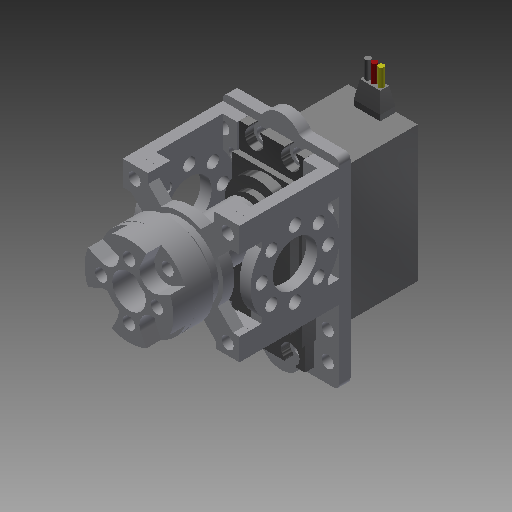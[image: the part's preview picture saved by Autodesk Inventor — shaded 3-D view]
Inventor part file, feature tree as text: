
AUTODESK INVENTOR PART (.ipt)
format: ipt  version: 2019 (Build 230136000, 136)  size: 800,768 bytes
history: native  units: in
note: dims shown in document units (in); Inventor stores cm internally (conversion verified against a paired STEP export)
features: extrude x23, sketch x23, other x11, projected_geometry x10, fillet x3, mirror x2, plane x1, pattern_circular x1
ambient origin geometry x8: Origin, YZ Plane, XZ Plane, XY Plane, X Axis, Y Axis, Z Axis, Center Point
bodies: Body1 (feature_tree), Body2 (feature_tree), Body3 (feature_tree), Body4 (feature_tree), Body5 (feature_tree), Body6 (feature_tree), Body7 (feature_tree), Body8 (feature_tree), Body9 (feature_tree), Body10 (feature_tree)
feature tree (74):
  other  "Servo"
  extrude  "Extrusion1"  Depth=1.525in
  extrude  "Extrusion2"  Depth=0.025in
  extrude  "Extrusion3"  Depth=0.17in
  fillet  "Fillet1"  Radius=0.11in
  plane  "Work Plane1"
  extrude  "Extrusion4"  Depth=0.07in
  fillet  "Fillet2"  Radius=0.07in
  mirror  "Mirror1"
  extrude  "Extrusion5"  [1 undecoded]
  extrude  "Extrusion6"  Depth=0.28in
  extrude  "Extrusion7"  Depth=0.1in
  extrude  "Extrusion8"  Depth=0.1in TaperAngle=0.0deg
  extrude  "Extrusion9"  Depth=0.3in
  extrude  "Extrusion10"  Depth=0.01in
  fillet  "Fillet3"  Radius=0.0625in
  extrude  "Extrusion11"  Depth=0.0625in
  extrude  "Extrusion12"  Depth=0.0625in
  extrude  "Extrusion13"  Depth=0.2in TaperAngle=0.0deg
  extrude  "Extrusion14"  Depth=0.0625in
  extrude  "Extrusion15"  Depth=0.2in
  extrude  "Extrusion16"  Depth=0.125in
  mirror  "Mirror2"
  extrude  "Extrusion18"  Depth=0.25in
  extrude  "Extrusion19"  Depth=0.125in
  extrude  "Extrusion20"  Depth=0.1325in
  extrude  "Extrusion21"  Depth=1.3125in
  extrude  "Extrusion22"  Depth=0.125in TaperAngle=0.0deg
  extrude  "Extrusion23"  Depth=0.125in
  extrude  "Extrusion24"  Depth=0.083in
  pattern_circular  "Circular Pattern1"  [2 undecoded]
  sketch  "Sketch1"  dims[d0=0.782in d1=1.525in]
  sketch  "Sketch2"  dims[d2=1.305in d3=0.0in d4=0.025in]
  sketch  "Sketch3"  dims[d5=0.025in d6=0.17in d7=0.11in d8=0.0in]
  sketch  "Sketch4"  dims[d9=0.508in d11=0.391in d12=0.07in d13=0.0in]
  sketch  "Sketch5"  dims[d14=0.366in d15=-0.16in]
  sketch  "Sketch6"  dims[d16=0.737in d18=0.28in]
  sketch  "Sketch7"  dims[d19=0.1in d20=0.21in d21=0.165in]
  other  "Red wire"
  sketch  "Sketch8"  dims[d22=0.165in d23=0.1in d24=0.0in]
  sketch  "Sketch9"  dims[d25=0.01in d26=0.3in]
  other  "Yellow Wire"
  sketch  "Sketch10"  dims[d27=0.17in d28=0.01in d29=0.0625in d30=0.0in]
  other  "BaseStructure"
  sketch  "Sketch11"  dims[d31=0.2in d32=-0.0687in d33=0.0625in]
  other  "ServoOutput"
  sketch  "Sketch12"  dims[d34=0.2in d35=0.0in d36=0.0625in]
  other  "SideStructure"
  sketch  "Sketch13"  dims[d37=0.04in d38=0.2in d39=0.0in]
  sketch  "Sketch14"  dims[d40=0.0625in d41=0.04in]
  projected_geometry  "Projected Loop1"
  projected_geometry  "Projected Loop2"
  sketch  "Sketch16"  dims[d42=0.2in d43=0.0in d44=0.136in]
  sketch  "Sketch17"  dims[d47=2.25in d48=0.125in]
  other  "Pattern of SideStructure:1"
  other  "SideStructureMirror"
  sketch  "Sketch18"  dims[d49=0.25in d50=0.25in]
  projected_geometry  "Projected Loop3"
  projected_geometry  "Projected Loop4"
  projected_geometry  "Projected Loop5"
  projected_geometry  "Projected Loop6"
  projected_geometry  "Projected Loop7"
  other  "BearingStructure"
  sketch  "Sketch19"  dims[d51=0.125in d52=0.2165in]
  sketch  "Sketch20"  dims[d53=0.1325in d54=0.1325in]
  other  "HubShaft"
  sketch  "Sketch21"  dims[d55=1.3125in d56=0.3125in]
  sketch  "Sketch22"  dims[d57=0.435in d58=0.125in d59=0.0in]
  sketch  "Sketch23"  dims[d60=0.0625in d61=0.125in]
  other  "HubAdapter"
  sketch  "Sketch24"  dims[d62=0.0625in d63=0.0in d66=0.083in d67=0.083in d68=0.125in d69=0.125in d70=0.125in d71=0.0in d72=0.125in d73=0.75in d74=0.0in d75=0.125in d76=0.0in d80=1.0in d82=0.125in d83=0.0in d84=0.5in d85=0.75in d86=0.136in d87=3.1496in d89=360.0deg d91=0.125in d92=0.0in d93=0.95in d94=45.0deg d96=0.26in d97=0.13in d100=45.0deg d101=0.13in d102=0.26in d103=0.125in d104=0.0in d105=0.845in d106=0.072in d107=0.0in d108=0.5in d109=0.8575in d110=0.0in d111=1.0in d112=0.75in d113=0.136in d114=3.1496in d116=360.0deg d118=0.2in d119=0.0in d120=0.3in d121=0.2in d122=0.0in d123=0.375in d124=0.625in d125=0.136in d126=1.5748in d128=360.0deg d130=0.25in d131=0.0in d133=0.1374in d134=0.1374in d135=0.168in d136=0.0in d137=1.5748in d138=360.0deg]
  projected_geometry  "Project Cut Edges1"
  projected_geometry  "Project Cut Edges2"
  projected_geometry  "Project Cut Edges3"
note: 3 required parameter values undecoded (feature->parameter linkage not recoverable at this tier; creation-order binding heuristic only, values carry confidence <= 0.55)
